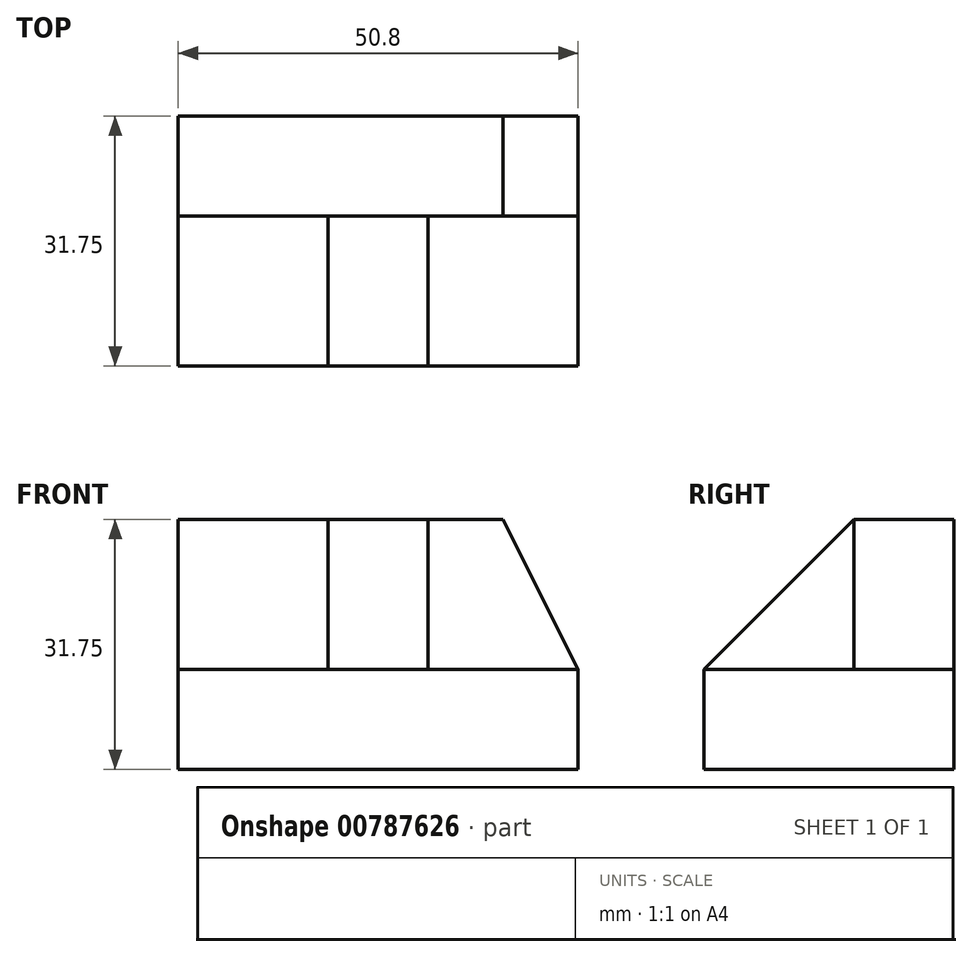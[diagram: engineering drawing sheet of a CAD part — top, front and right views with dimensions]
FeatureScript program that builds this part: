
annotation { "Feature Type Name" : "Feature", "Feature Type Description" : "" }
export const myFeature = defineFeature(function(context is Context, id is Id, definition is map)
    precondition{}
    {
        {
            var Q0;
            Q0=qCreatedBy(makeId("Front.planeOp"),FACE);
            var sketch = newSketch(context, id + "F0", { "sketchPlane" : qUnion([Q0])});
            skLineSegment(sketch, "E0", {"start": v(0, 0) * mm, "end": v(50.8, 0) * mm});
            skLineSegment(sketch, "E1", {"start": v(50.8, 0) * mm, "end": v(50.8, 31.75) * mm});
            skLineSegment(sketch, "E2", {"start": v(50.8, 31.75) * mm, "end": v(0, 31.75) * mm});
            skLineSegment(sketch, "E3", {"start": v(0, 31.75) * mm, "end": v(0, 0) * mm});
            skSolve(sketch);
        }
        {
            var Q0;
            Q0 = qSketchRegion(id + "F0", true);
            extrude(context, id + "F1", {"entities" : qUnion([Q0]), "depth" : 31.75 * mm, "offsetDistance" : 25.4 * mm});
        }
        {
            var Q0;
            Q0=makeQuery(id+"F1.opExtrude","SWEPT_FACE",FACE,{"disambiguationData":[OSD([sQuery(id+"F0.wireOp",EDGE,"E1")])]});
            var sketch = newSketch(context, id + "F2", { "sketchPlane" : qUnion([Q0])});
            skLineSegment(sketch, "E4", {"start": v(-31.75, 0) * mm, "end": v(-31.75, 12.7) * mm});
            skLineSegment(sketch, "E5", {"start": v(-31.75, 12.7) * mm, "end": v(-12.7, 12.7) * mm});
            skLineSegment(sketch, "E6", {"start": v(-12.7, 12.7) * mm, "end": v(-12.7, 31.75) * mm});
            skSolve(sketch);
        }
        {
            var Q0;
            Q0 = qSketchRegion(id + "F2", true);
            var Q1;
            {var subQ0=sQuery(id+"F2.wireOp",EDGE,"E5");Q1=makeQuery(id+"F2.imprint","IMPRINT",FACE,{"disambiguationData":[TD([[makeQuery(id+"F2.imprint","IMPRINT",EDGE,{"derivedFrom":subQ0}),1.0]])]});}
            extrude(context, id + "F3", {"entities" : qUnion([Q0, Q1]), "operationType" : NewBodyOperationType.REMOVE, "oppositeDirection" : true, "depth" : 19.05 * mm, "offsetDistance" : 25.4 * mm});
        }
        {
            var Q0;
            Q0=makeQuery(id+"F1.opExtrude","SWEPT_FACE",FACE,{"disambiguationData":[OSD([sQuery(id+"F0.wireOp",EDGE,"E3")])]});
            var sketch = newSketch(context, id + "F4", { "sketchPlane" : qUnion([Q0])});
            skLineSegment(sketch, "E7", {"start": v(31.75, 0) * mm, "end": v(31.75, 12.7) * mm});
            skLineSegment(sketch, "E8", {"start": v(31.75, 12.7) * mm, "end": v(12.7, 12.7) * mm});
            skLineSegment(sketch, "E9", {"start": v(12.7, 12.7) * mm, "end": v(12.7, 31.75) * mm});
            skLineSegment(sketch, "E10", {"start": v(12.7, 31.75) * mm, "end": v(31.75, 31.75) * mm});
            skLineSegment(sketch, "E11", {"start": v(31.75, 31.75) * mm, "end": v(31.75, 12.7) * mm});
            skSolve(sketch);
        }
        {
            var Q0;
            Q0=makeQuery(id+"F4.imprint","IMPRINT",FACE,{"disambiguationData":[TD([[makeQuery(id+"F4.imprint","IMPRINT",EDGE,{"derivedFrom":sQuery(id+"F4.wireOp",EDGE,"E8")}),-1.0]])]});
            extrude(context, id + "F5", {"entities" : qUnion([Q0]), "operationType" : NewBodyOperationType.REMOVE, "oppositeDirection" : true, "depth" : 19.05 * mm, "offsetDistance" : 25.4 * mm});
        }
        {
            var Q0;
            Q0=makeQuery(id+"F3.boolean.opBoolean","COPY",FACE,{"derivedFrom":makeQuery(id+"F3.opExtrude","SWEPT_FACE",FACE,{"disambiguationData":[OSD([sQuery(id+"F2.wireOp",EDGE,"E6")])]})});
            var sketch = newSketch(context, id + "F6", { "sketchPlane" : qUnion([Q0])});
            skLineSegment(sketch, "E12", {"start": v(31.75, 31.75) * mm, "end": v(41.27, 31.75) * mm});
            skLineSegment(sketch, "E13", {"start": v(41.27, 31.75) * mm, "end": v(50.8, 12.7) * mm});
            skLineSegment(sketch, "E14", {"start": v(50.8, 12.7) * mm, "end": v(50.8, 31.75) * mm});
            skLineSegment(sketch, "E15", {"start": v(50.8, 31.75) * mm, "end": v(41.27, 31.75) * mm});
            skSolve(sketch);
        }
        {
            var Q0;
            Q0=makeQuery(id+"F6.imprint","IMPRINT",FACE,{"disambiguationData":[TD([[makeQuery(id+"F6.imprint","IMPRINT",EDGE,{"derivedFrom":sQuery(id+"F6.wireOp",EDGE,"E13")}),1.0]])]});
            extrude(context, id + "F7", {"entities" : qUnion([Q0]), "operationType" : NewBodyOperationType.REMOVE, "oppositeDirection" : true, "depth" : 12.7 * mm, "offsetDistance" : 25.4 * mm});
        }
        {
            var Q0;
            Q0=makeQuery(id+"F3.boolean.opBoolean","COPY",FACE,{"derivedFrom":makeQuery(id+"F3.opExtrude","CAP_FACE",FACE,{"disambiguationData":[OSD([sQuery(id+"F0.wireOp",EDGE,"E1"),sQuery(id+"F0.wireOp",EDGE,"E2"),sQuery(id+"F2.wireOp",EDGE,"E5"),sQuery(id+"F2.wireOp",EDGE,"E6")])],"isStart":false})});
            var sketch = newSketch(context, id + "F8", { "sketchPlane" : qUnion([Q0])});
            skLineSegment(sketch, "E16", {"start": v(-12.7, 31.75) * mm, "end": v(-31.75, 12.7) * mm});
            skLineSegment(sketch, "E17", {"start": v(-31.75, 12.7) * mm, "end": v(-31.75, 31.75) * mm});
            skLineSegment(sketch, "E18", {"start": v(-31.75, 31.75) * mm, "end": v(-12.7, 31.75) * mm});
            skSolve(sketch);
        }
        {
            var Q0;
            Q0=makeQuery(id+"F8.imprint","IMPRINT",FACE,{"disambiguationData":[TD([[makeQuery(id+"F8.imprint","IMPRINT",EDGE,{"derivedFrom":sQuery(id+"F8.wireOp",EDGE,"E16")}),-1.0]])]});
            extrude(context, id + "F9", {"entities" : qUnion([Q0]), "operationType" : NewBodyOperationType.REMOVE, "oppositeDirection" : true, "depth" : 12.7 * mm, "offsetDistance" : 25.4 * mm});
        }
    });
